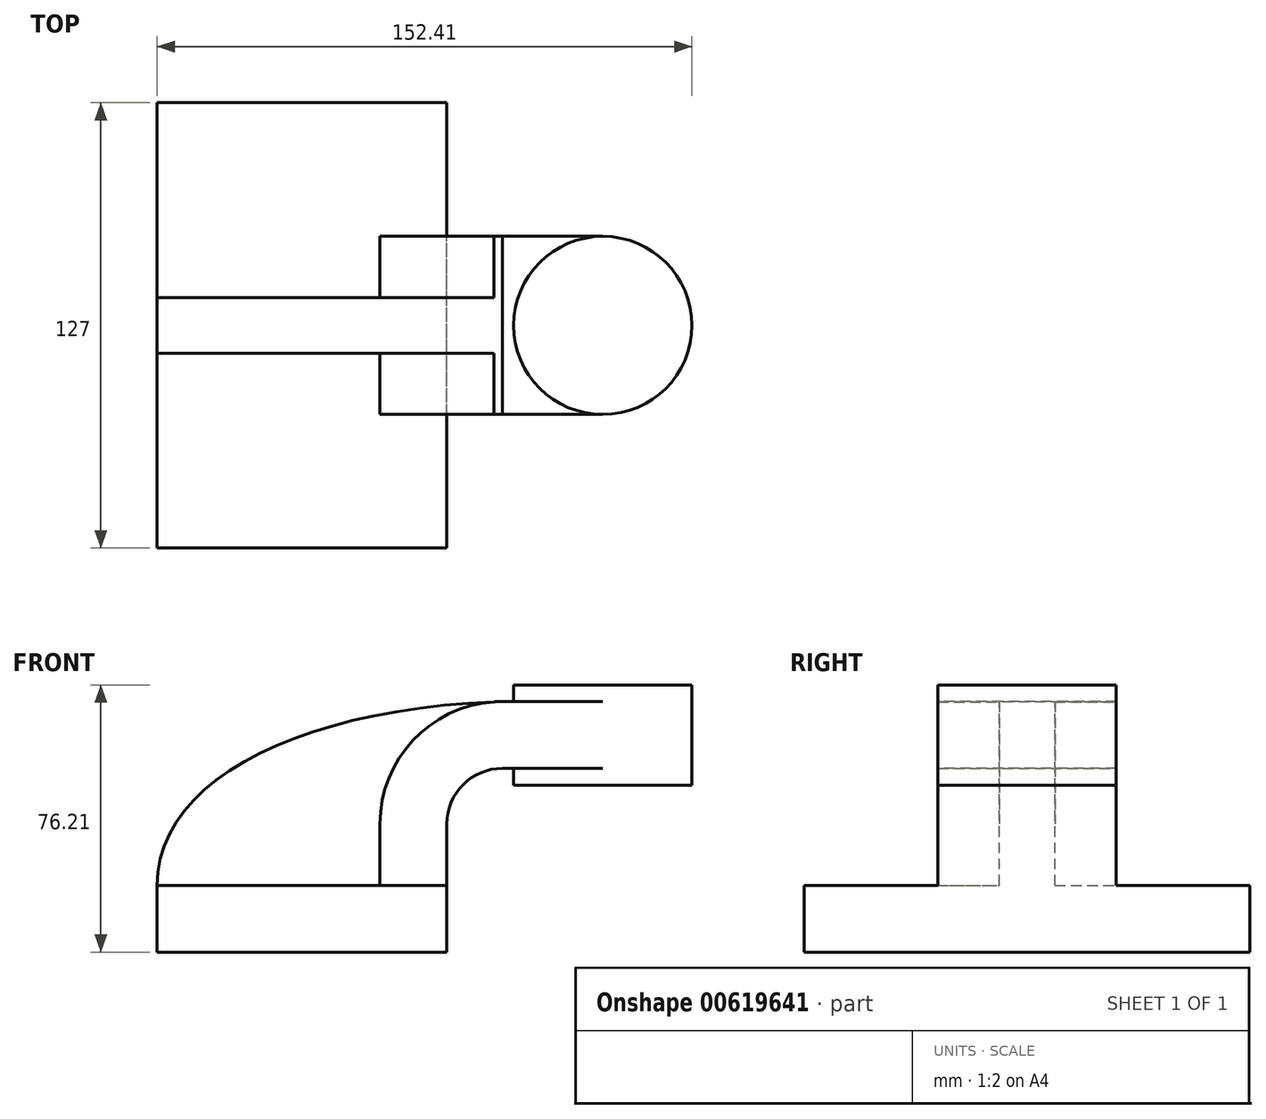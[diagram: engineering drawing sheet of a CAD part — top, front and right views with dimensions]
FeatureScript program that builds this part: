
annotation { "Feature Type Name" : "Feature", "Feature Type Description" : "" }
export const myFeature = defineFeature(function(context is Context, id is Id, definition is map)
    precondition{}
    {
        {
            var Q0;
            Q0=qCreatedBy(makeId("Front.planeOp"),FACE);
            var sketch = newSketch(context, id + "F0", { "sketchPlane" : qUnion([Q0])});
            skLineSegment(sketch, "E0.bottom", {"start": v(41.28, 9.53) * mm, "end": v(-41.28, 9.53) * mm});
            skLineSegment(sketch, "E0.top", {"start": v(41.28, -9.52) * mm, "end": v(-41.28, -9.52) * mm});
            skLineSegment(sketch, "E0.left", {"start": v(41.28, 9.53) * mm, "end": v(41.28, -9.52) * mm});
            skLineSegment(sketch, "E0.right", {"start": v(-41.28, 9.53) * mm, "end": v(-41.28, -9.52) * mm});
            skPoint(sketch, "E0.middle", {"position": v(0, 0) * mm});
            skLineSegment(sketch, "E1.bottom", {"start": v(111.12, 66.68) * mm, "end": v(60.33, 66.68) * mm});
            skLineSegment(sketch, "E1.top", {"start": v(111.12, 38.1) * mm, "end": v(60.33, 38.1) * mm});
            skLineSegment(sketch, "E1.left", {"start": v(111.13, 66.68) * mm, "end": v(111.13, 38.1) * mm});
            skLineSegment(sketch, "E1.right", {"start": v(60.33, 66.68) * mm, "end": v(60.33, 38.1) * mm});
            skPoint(sketch, "E1.middle", {"position": v(85.73, 52.39) * mm});
            skLineSegment(sketch, "E2", {"start": v(41.28, 9.53) * mm, "end": v(41.28, 27) * mm});
            skArc(sketch, "E3", {"start": v(41.27, 27) * mm, "mid": v(45.92, 38.23) * mm, "end": v(57.15, 42.88) * mm});
            skLineSegment(sketch, "E4", {"start": v(57.15, 42.88) * mm, "end": v(85.73, 42.88) * mm});
            skPoint(sketch, "E4.endSnap0", {"position": v(85.73, 38.1) * mm});
            skLineSegment(sketch, "E5.0", {"start": v(57.15, 61.93) * mm, "end": v(85.73, 61.93) * mm});
            skArc(sketch, "E5.1", {"start": v(22.22, 27) * mm, "mid": v(32.45, 51.7) * mm, "end": v(57.15, 61.93) * mm});
            skLineSegment(sketch, "E5.2", {"start": v(22.22, 9.53) * mm, "end": v(22.22, 27) * mm});
            skFitSpline(sketch, "E6", {"points": [v(-41.28, 9.53) * mm, v(57.15, 61.93) * mm], "startDerivative": vector(-0.29, 90.33) * mm, "endDerivative": vector(171.45, 5.23) * mm});
            skLineSegment(sketch, "E7", {"start": v(85.73, 66.68) * mm, "end": v(85.73, 38.1) * mm});
            skSolve(sketch);
        }
        {
            var Q0;
            Q0=makeQuery(id+"F0.imprint","IMPRINT",FACE,{"disambiguationData":[TD([[makeQuery(id+"F0.imprint","IMPRINT",EDGE,{"derivedFrom":sQuery(id+"F0.wireOp",EDGE,"E0.top")}),-1.0]])]});
            extrude(context, id + "F1", {"entities" : qUnion([Q0]), "endBound" : BoundingType.SYMMETRIC, "depth" : 127 * mm, "offsetDistance" : 25.4 * mm});
        }
        {
            var Q0;
            {var subQ1=sQuery(id+"F0.wireOp",EDGE,"E2");Q0=makeQuery(id+"F0.imprint","IMPRINT",FACE,{"disambiguationData":[TD([[makeQuery(id+"F0.imprint","IMPRINT",EDGE,{"derivedFrom":subQ1}),1.0]])]});}
            var Q1;
            {var subQ0=sQuery(id+"F0.wireOp",EDGE,"E5.0");var subQ1=sQuery(id+"F0.wireOp",EDGE,"E1.right");var subQ2=makeQuery(id+"F0.imprint","INTERSECT",VERTEX,{"derivedFrom":[subQ1,subQ0]});Q1=makeQuery(id+"F0.imprint","IMPRINT",FACE,{"disambiguationData":[TD([[makeQuery(id+"F0.imprint","IMPRINT",EDGE,{"disambiguationData":[TD([[subQ2,-1.0]])],"derivedFrom":subQ1}),1.0]])]});}
            var Q2;
            Q2 = qConstructionFilter(qBodyType(qCreatedBy(id + "F0" ,EDGE), BodyType.WIRE), ConstructionObject.NO);
            extrude(context, id + "F2", {"entities" : qUnion([Q0, Q1]), "operationType" : NewBodyOperationType.ADD, "surfaceEntities" : qUnion([Q2]), "endBound" : BoundingType.SYMMETRIC, "depth" : 50.8 * mm, "offsetDistance" : 25.4 * mm});
        }
        {
            var Q0;
            {var subQ3=sQuery(id+"F0.wireOp",EDGE,"E5.2");Q0=makeQuery(id+"F0.imprint","IMPRINT",FACE,{"disambiguationData":[TD([[makeQuery(id+"F0.imprint","IMPRINT",EDGE,{"derivedFrom":subQ3}),1.0]])]});}
            extrude(context, id + "F3", {"entities" : qUnion([Q0]), "operationType" : NewBodyOperationType.ADD, "endBound" : BoundingType.SYMMETRIC, "depth" : 15.88 * mm, "offsetDistance" : 25.4 * mm});
        }
        {
            var Q0;
            {var subQ4=sQuery(id+"F0.wireOp",EDGE,"E1.left");Q0=makeQuery(id+"F0.imprint","IMPRINT",FACE,{"disambiguationData":[TD([[makeQuery(id+"F0.imprint","IMPRINT",EDGE,{"derivedFrom":subQ4}),-1.0]])]});}
            var Q1;
            Q1=sQuery(id+"F0.wireOp",EDGE,"E7");
            revolve(context, id + "F4", {"operationType" : NewBodyOperationType.ADD, "entities" : qUnion([Q0]), "axis" : qUnion([Q1]), "revolveType" : RevolveType.FULL});
        }
    });
